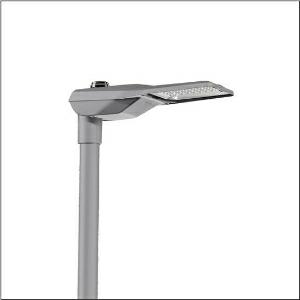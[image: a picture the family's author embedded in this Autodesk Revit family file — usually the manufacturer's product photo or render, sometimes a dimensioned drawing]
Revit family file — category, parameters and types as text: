
# Revit family: streetlight_sl_21_mini___p0_8a_5xe6u67n08gb_cd46
name_source: partatom
category: Lighting Fixtures
units: mm (PartAtom-declared; Revit-internal decimal feet)

## family parameters
Cut with Voids When Loaded = No
Host = Face
Light Source = No
Part Type = Normal
Room Calculation Point = No
Round Connector Dimension = Use Diameter
Shared = No

## types (1)
- --- (1 x LED, 5370 lm, 40.4 W, 2700K)
    Apparent Load = 40 VA
    CIE Flux Codes = 33 69 96 100 100
    Color Rendering = 70
    Color Temperature = 2700K
    Default Elevation = 1800 mm
    Description = Streetlight SL 21 mini, mast luminaire, primary light control with lens, of PMMA, primary optical cover: cover, of toughened safety glass, transparent, light distribution: P0.8a, light emission: direct distribution, primary light characteristic: asymmetric, installation type: side-entry, LED, 3G 1.5mm², High Power LED, rated luminous flux: 5.370lm, luminous efficacy: 133lm/W, light colour: 727, colour temperature: 2700K, control gear: NEMA (7pin), control: flexible luminous flux parameterisation, time-dependent luminous flux control, constant luminous flux control, pre-setting: linear dimming characteristic, overheat protection, mains connection: 230..240V, AC, 50/60Hz, connection cable pre-assembled, cable length: 8,5m, wiring characteristics: H07RN-F, start of lifetime: 40W, end of service life: 41W, reduction: 19W, luminaire housing, of diecast aluminium (EN AC-44300), powder-coated, Siteco® metallic grey (DB 702S), corrosivity category C5 mid according to DIN EN ISO 12944, multi-level sealing system, sealing non-destructively replaceable, inclination adjustable: 0°, 5°, 10°, 15°, length: 628mm, width: 235mm, height: 110mm, spigot size: 42mm (side-entry), mounting height: 4..8m, protection rating (complete): IP66, insulation class (complete): insulation class I (protective earthing), certification: CE, ENEC, ENEC+, VDE, impact resistance: IK10, permissible operating ambient temperature for outdoor applications: -40..+50°C, standard-compliant lighting for roads and squares, packaging unit: 1 piece

Light Distribution: P0.8a
    Height = 110 mm
    Lamp = 1 x LED
    Lamp Light Flux = 5370 lm
    Lamp Power = 40.4 W
    Lamp count = 1
    Length = 625 mm
    Luminous efficacy = 133 lm/W
    Manufacturer = Siteco
    ModVariant = No
    Model = 5XE6U67N08GB
    Number of Poles = 1
    OnlyDefault = Yes
    Power Factor = 1
    Product Name = Streetlight SL 21 mini | P0.8a
    Product group = mast luminaire | pylon top
    ProductGroupID = 6100
    Protection Class = Protection class I
    Protection Degree = IP 66
    RLX_Detail_Level = 1
    RLX_Emergency_Light_Flux = 0 lm
    RLX_Emergency_Type = 0
    RLX_Emergency_Type_DB = No
    RlxData = <blob elided: 91561 chars, md5=30a9019b>
    Socket = socket
    Standby Power = 0 W
    System Light Flux = 5370 lm
    System Power = 40 W
    Type Comments = factory setting: luminous flux: 100 % | dim-lin: 254 | 812 mA
    Type Image = l_1294379.jpg
    URL = http://relux.com
    VarID = @adj_094949
    Voltage = 0 V
    Weight = 0.00 kg
    Width = 234 mm

## geometry (parser evidence)
native form markers: Blend x4, Sweep x11
no freeform markers — native parametric forms only
